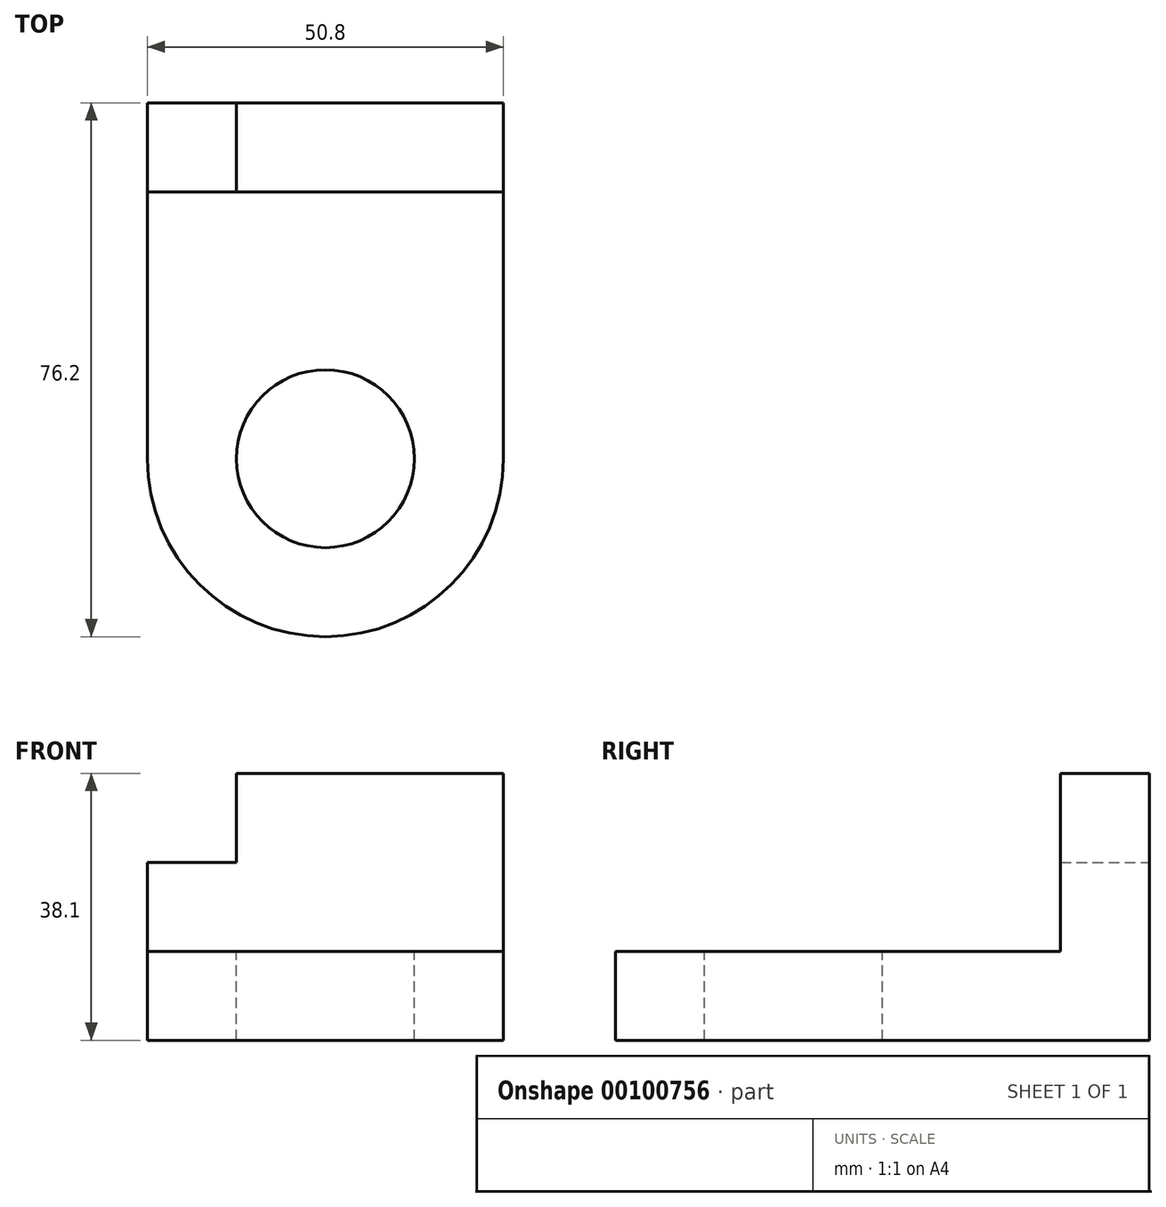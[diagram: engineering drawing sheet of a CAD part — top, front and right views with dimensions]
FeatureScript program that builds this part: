
annotation { "Feature Type Name" : "Feature", "Feature Type Description" : "" }
export const myFeature = defineFeature(function(context is Context, id is Id, definition is map)
    precondition{}
    {
        {
            var Q0;
            Q0=qCreatedBy(makeId("Top.planeOp"),FACE);
            var sketch = newSketch(context, id + "F0", { "sketchPlane" : qUnion([Q0])});
            skLineSegment(sketch, "E0.bottom", {"start": v(25.4, -38.1) * mm, "end": v(-25.4, -38.1) * mm});
            skLineSegment(sketch, "E0.top", {"start": v(25.4, 38.1) * mm, "end": v(-25.4, 38.1) * mm});
            skLineSegment(sketch, "E0.left", {"start": v(25.4, -38.1) * mm, "end": v(25.4, 38.1) * mm});
            skLineSegment(sketch, "E0.right", {"start": v(-25.4, -38.1) * mm, "end": v(-25.4, 38.1) * mm});
            skPoint(sketch, "E0.middle", {"position": v(0, 0) * mm});
            skSolve(sketch);
        }
        {
            var Q0;
            Q0=makeQuery(id+"F0.imprint","IMPRINT",FACE,{"disambiguationData":[TD([[makeQuery(id+"F0.imprint","IMPRINT",EDGE,{"derivedFrom":sQuery(id+"F0.wireOp",EDGE,"E0.bottom")}),-1.0]])]});
            extrude(context, id + "F1", {"entities" : qUnion([Q0]), "depth" : 12.7 * mm});
        }
        {
            var Q0;
            Q0=makeQuery(id+"F1.opExtrude","CAP_FACE",FACE,{"disambiguationData":[OSD([sQuery(id+"F0.wireOp",EDGE,"E0.bottom"),sQuery(id+"F0.wireOp",EDGE,"E0.left"),sQuery(id+"F0.wireOp",EDGE,"E0.right"),sQuery(id+"F0.wireOp",EDGE,"lZeZWJxt-9Axn-us5S-VImz-v0ifg23OD0zY.bottom")])],"isStart":false});
            var sketch = newSketch(context, id + "F2", { "sketchPlane" : qUnion([Q0])});
            skLineSegment(sketch, "E1.bottom", {"start": v(-25.4, 38.1) * mm, "end": v(25.4, 38.1) * mm});
            skLineSegment(sketch, "E1.top", {"start": v(-25.4, 25.4) * mm, "end": v(25.4, 25.4) * mm});
            skLineSegment(sketch, "E1.left", {"start": v(-25.4, 38.1) * mm, "end": v(-25.4, 25.4) * mm});
            skLineSegment(sketch, "E1.right", {"start": v(25.4, 38.1) * mm, "end": v(25.4, 25.4) * mm});
            skSolve(sketch);
        }
        {
            var Q0;
            Q0=makeQuery(id+"F2.imprint","IMPRINT",FACE,{"disambiguationData":[TD([[makeQuery(id+"F2.imprint","IMPRINT",EDGE,{"derivedFrom":sQuery(id+"F2.wireOp",EDGE,"E1.bottom")}),1.0]])]});
            extrude(context, id + "F3", {"entities" : qUnion([Q0]), "operationType" : NewBodyOperationType.ADD, "depth" : 25.4 * mm});
        }
        {
            var Q0;
            Q0=makeQuery(id+"F3.opExtrude","CAP_FACE",FACE,{"disambiguationData":[OSD([sQuery(id+"F2.wireOp",EDGE,"E1.bottom"),sQuery(id+"F2.wireOp",EDGE,"E1.top"),sQuery(id+"F2.wireOp",EDGE,"E1.left"),sQuery(id+"F2.wireOp",EDGE,"E1.right")])],"isStart":false});
            var sketch = newSketch(context, id + "F4", { "sketchPlane" : qUnion([Q0])});
            skLineSegment(sketch, "E2.bottom", {"start": v(-25.4, 25.4) * mm, "end": v(-12.7, 25.4) * mm});
            skLineSegment(sketch, "E2.top", {"start": v(-25.4, 38.1) * mm, "end": v(-12.7, 38.1) * mm});
            skLineSegment(sketch, "E2.left", {"start": v(-25.4, 38.1) * mm, "end": v(-25.4, 25.4) * mm});
            skLineSegment(sketch, "E2.right", {"start": v(-12.7, 38.1) * mm, "end": v(-12.7, 25.4) * mm});
            skSolve(sketch);
        }
        {
            var Q0;
            Q0=makeQuery(id+"F4.imprint","IMPRINT",FACE,{"disambiguationData":[TD([[makeQuery(id+"F4.imprint","IMPRINT",EDGE,{"derivedFrom":sQuery(id+"F4.wireOp",EDGE,"E2.bottom")}),1.0]])]});
            extrude(context, id + "F5", {"entities" : qUnion([Q0]), "operationType" : NewBodyOperationType.REMOVE, "oppositeDirection" : true, "depth" : 12.7 * mm});
        }
        {
            var Q0;
            Q0=makeQuery(id+"F1.opExtrude","CAP_FACE",FACE,{"disambiguationData":[OSD([sQuery(id+"F0.wireOp",EDGE,"E0.bottom"),sQuery(id+"F0.wireOp",EDGE,"E0.left"),sQuery(id+"F0.wireOp",EDGE,"E0.right"),sQuery(id+"F0.wireOp",EDGE,"lZeZWJxt-9Axn-us5S-VImz-v0ifg23OD0zY.bottom")])],"isStart":false});
            var sketch = newSketch(context, id + "F6", { "sketchPlane" : qUnion([Q0])});
            skCircle(sketch, "E3", {"center": v(0, -12.7) * mm, "radius": 12.7 * mm});
            skArc(sketch, "E4", {"start": v(-25.4, -12.7) * mm, "mid": v(0, -38.1) * mm, "end": v(25.4, -12.7) * mm});
            skSolve(sketch);
        }
        {
            var Q0;
            Q0=makeQuery(id+"F6.imprint","IMPRINT",FACE,{"disambiguationData":[TD([[makeQuery(id+"F6.imprint","IMPRINT",EDGE,{"derivedFrom":sQuery(id+"F6.wireOp",EDGE,"E3")}),1.0]])]});
            var Q1;
            {var subQ0=sQuery(id+"F6.wireOp",EDGE,"E4");var subQ1=makeQuery(id+"F1.opExtrude","CAP_EDGE",EDGE,{"disambiguationData":[OSD([sQuery(id+"F0.wireOp",EDGE,"E0.right")])],"isStart":false});var subQ2=makeQuery(id+"F6.imprint","INTERSECT",VERTEX,{"derivedFrom":[subQ1,subQ0]});Q1=makeQuery(id+"F6.imprint","IMPRINT",FACE,{"disambiguationData":[TD([[makeQuery(id+"F6.imprint","IMPRINT",EDGE,{"disambiguationData":[TD([[subQ2,-1.0]])],"derivedFrom":subQ0}),-1.0]])]});}
            var Q2;
            {var subQ0=sQuery(id+"F6.wireOp",EDGE,"E4");var subQ1=makeQuery(id+"F1.opExtrude","CAP_EDGE",EDGE,{"disambiguationData":[OSD([sQuery(id+"F0.wireOp",EDGE,"E0.left")])],"isStart":false});var subQ2=makeQuery(id+"F6.imprint","INTERSECT",VERTEX,{"derivedFrom":[subQ1,subQ0]});Q2=makeQuery(id+"F6.imprint","IMPRINT",FACE,{"disambiguationData":[TD([[makeQuery(id+"F6.imprint","IMPRINT",EDGE,{"disambiguationData":[TD([[subQ2,1.0]])],"derivedFrom":subQ0}),-1.0]])]});}
            extrude(context, id + "F7", {"entities" : qUnion([Q0, Q1, Q2]), "operationType" : NewBodyOperationType.REMOVE, "endBound" : BoundingType.THROUGH_ALL, "oppositeDirection" : true, "depth" : 25.4 * mm});
        }
    });
